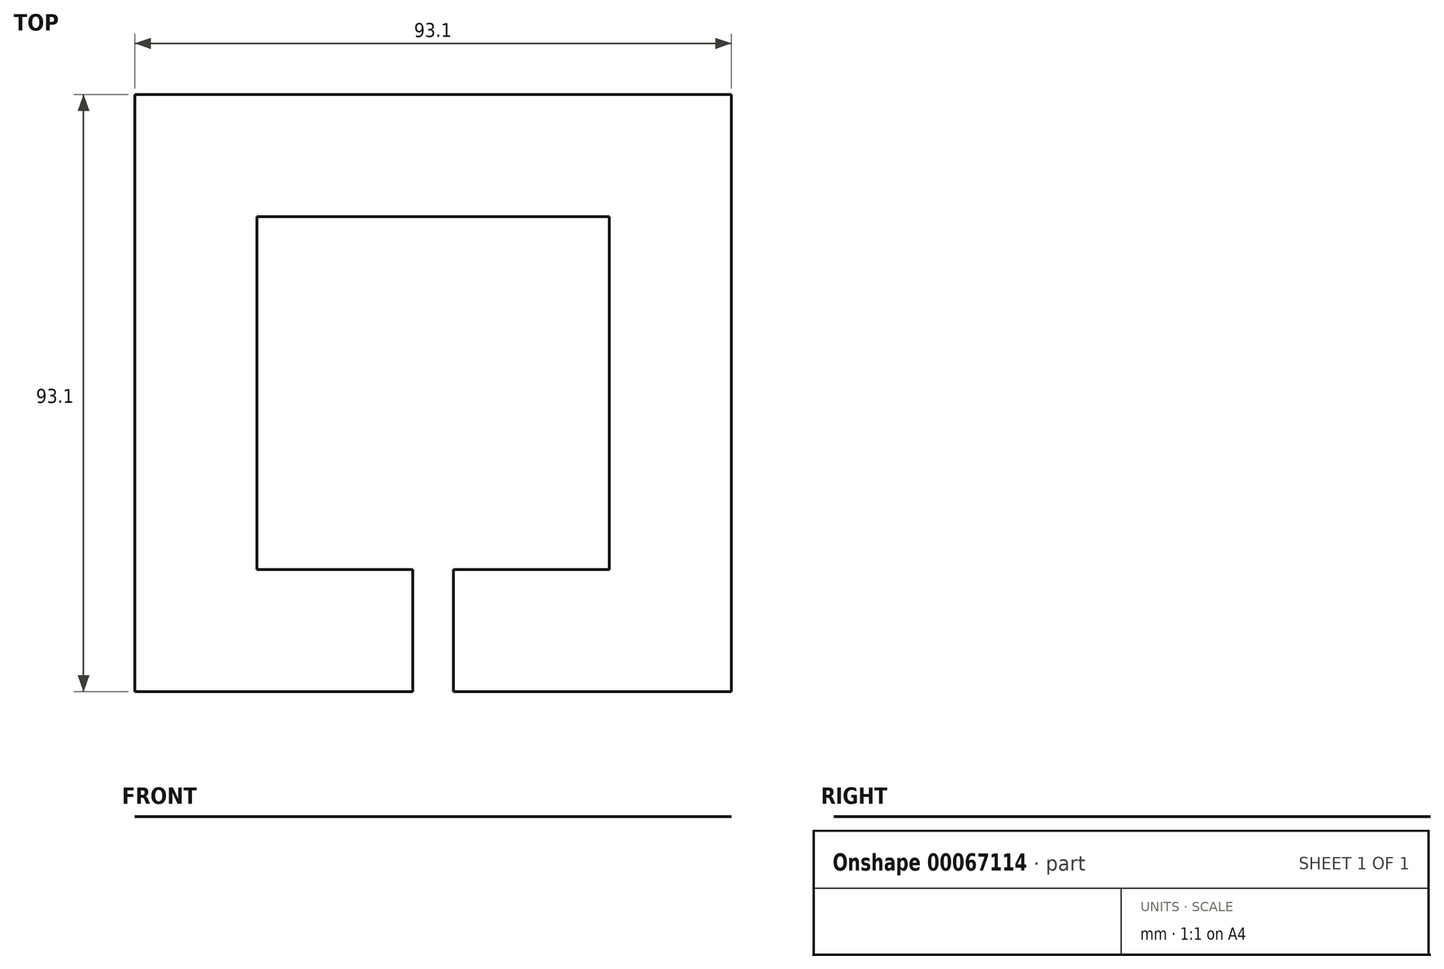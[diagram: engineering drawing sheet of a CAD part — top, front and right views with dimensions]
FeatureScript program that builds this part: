
annotation { "Feature Type Name" : "Feature", "Feature Type Description" : "" }
export const myFeature = defineFeature(function(context is Context, id is Id, definition is map)
    precondition{}
    {
        {
            var Q0;
            Q0=qCreatedBy(makeId("Top.planeOp"),FACE);
            var sketch = newSketch(context, id + "F0", { "sketchPlane" : qUnion([Q0])});
            skLineSegment(sketch, "E0.bottom", {"start": v(-46.55, 0) * mm, "end": v(46.55, 0) * mm});
            skLineSegment(sketch, "E0.top", {"start": v(-46.55, -93.1) * mm, "end": v(46.55, -93.1) * mm});
            skLineSegment(sketch, "E0.left", {"start": v(-46.55, 0) * mm, "end": v(-46.55, -93.1) * mm});
            skLineSegment(sketch, "E0.right", {"start": v(46.55, 0) * mm, "end": v(46.55, -93.1) * mm});
            skLineSegment(sketch, "E1.bottom", {"start": v(-27.5, -19.05) * mm, "end": v(27.5, -19.05) * mm});
            skLineSegment(sketch, "E1.top", {"start": v(-27.5, -74.05) * mm, "end": v(27.5, -74.05) * mm});
            skLineSegment(sketch, "E1.left", {"start": v(-27.5, -19.05) * mm, "end": v(-27.5, -74.05) * mm});
            skLineSegment(sketch, "E1.right", {"start": v(27.5, -19.05) * mm, "end": v(27.5, -74.05) * mm});
            skLineSegment(sketch, "E2", {"start": v(-27.5, -19.05) * mm, "end": v(-46.55, -19.05) * mm, "construction": true});
            skLineSegment(sketch, "E3", {"start": v(27.5, -19.05) * mm, "end": v(46.55, -19.05) * mm, "construction": true});
            skLineSegment(sketch, "E4", {"start": v(0, 0) * mm, "end": v(0, -19.05) * mm, "construction": true});
            skLineSegment(sketch, "E5.bottom", {"start": v(-3.17, -74.05) * mm, "end": v(3.17, -74.05) * mm});
            skLineSegment(sketch, "E5.top", {"start": v(-3.17, -93.1) * mm, "end": v(3.17, -93.1) * mm});
            skLineSegment(sketch, "E5.left", {"start": v(-3.17, -74.05) * mm, "end": v(-3.17, -93.1) * mm});
            skLineSegment(sketch, "E5.right", {"start": v(3.18, -74.05) * mm, "end": v(3.18, -93.1) * mm});
            skLineSegment(sketch, "E6", {"start": v(-3.17, -83.57) * mm, "end": v(-46.55, -83.57) * mm, "construction": true});
            skLineSegment(sketch, "E7", {"start": v(3.17, -83.57) * mm, "end": v(46.55, -83.57) * mm, "construction": true});
            skSolve(sketch);
        }
        {
            var Q0;
            Q0=makeQuery(id+"F0.imprint","IMPRINT",FACE,{"disambiguationData":[TD([[makeQuery(id+"F0.imprint","IMPRINT",EDGE,{"derivedFrom":sQuery(id+"F0.wireOp",EDGE,"E0.bottom")}),-1.0]])]});
            extrude(context, id + "F1", {"entities" : qUnion([Q0]), "depth" : 1 / 203.2 * mm});
        }
    });
